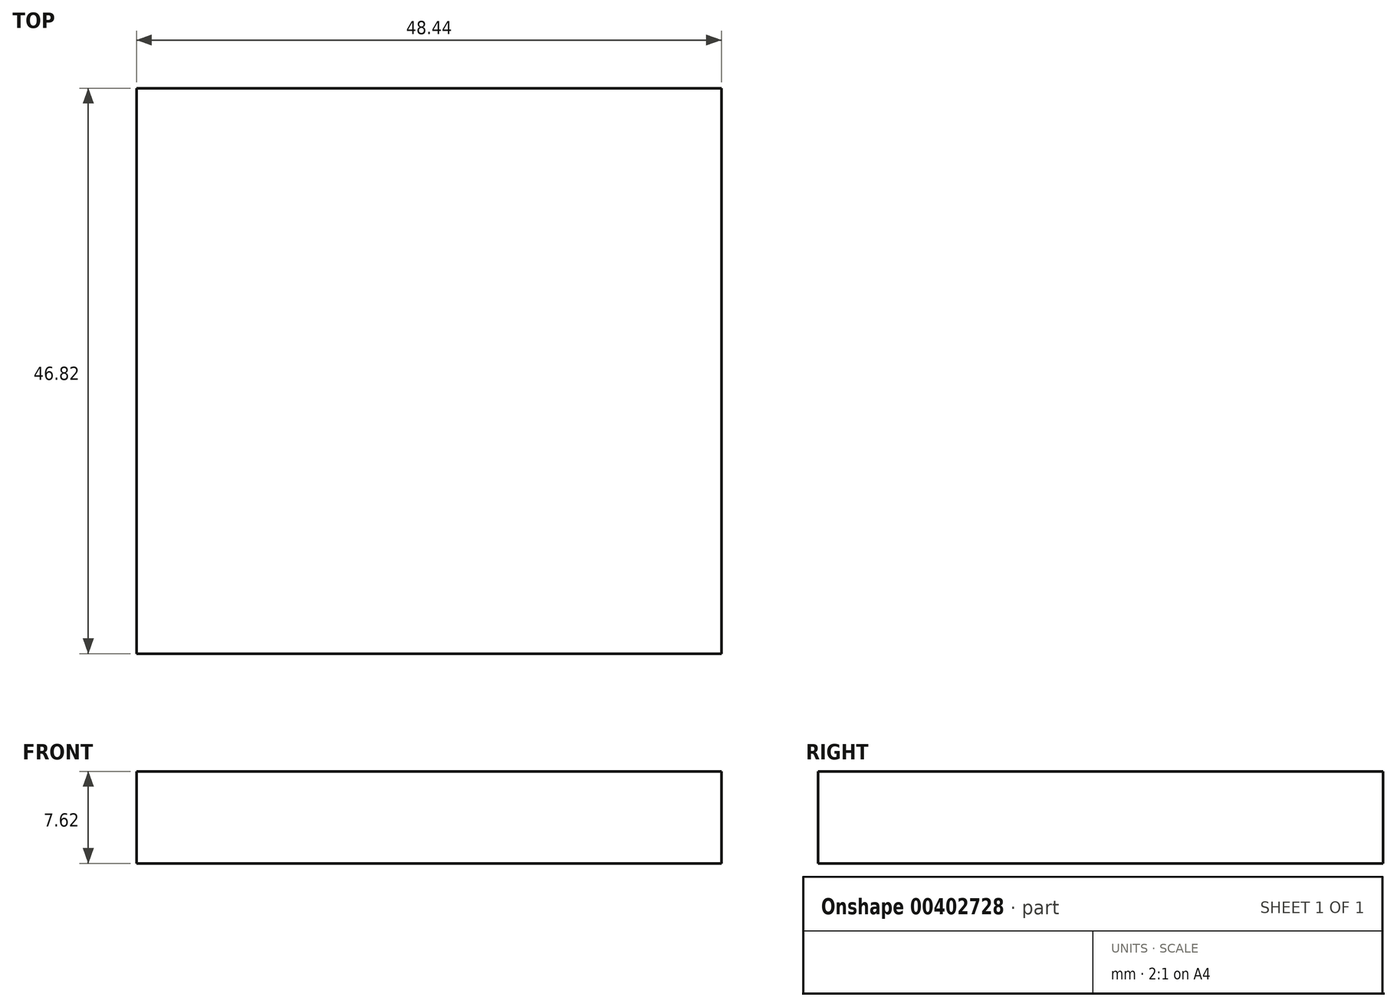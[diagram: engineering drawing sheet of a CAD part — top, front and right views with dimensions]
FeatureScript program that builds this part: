
annotation { "Feature Type Name" : "Feature", "Feature Type Description" : "" }
export const myFeature = defineFeature(function(context is Context, id is Id, definition is map)
    precondition{}
    {
        {
            var Q0;
            Q0=qCreatedBy(makeId("Top.planeOp"),FACE);
            var sketch = newSketch(context, id + "F0", { "sketchPlane" : qUnion([Q0])});
            skLineSegment(sketch, "E0.bottom", {"start": v(24.22, -23.41) * mm, "end": v(-24.22, -23.41) * mm});
            skLineSegment(sketch, "E0.top", {"start": v(24.22, 23.41) * mm, "end": v(-24.22, 23.41) * mm});
            skLineSegment(sketch, "E0.left", {"start": v(24.22, -23.41) * mm, "end": v(24.22, 23.41) * mm});
            skLineSegment(sketch, "E0.right", {"start": v(-24.22, -23.41) * mm, "end": v(-24.22, 23.41) * mm});
            skPoint(sketch, "E0.middle", {"position": v(0, 0) * mm});
            skSolve(sketch);
        }
        {
            var Q0;
            Q0 = qSketchRegion(id + "F0", true);
            extrude(context, id + "F1", {"entities" : qUnion([Q0]), "depth" : 7.62 * mm});
        }
    });
